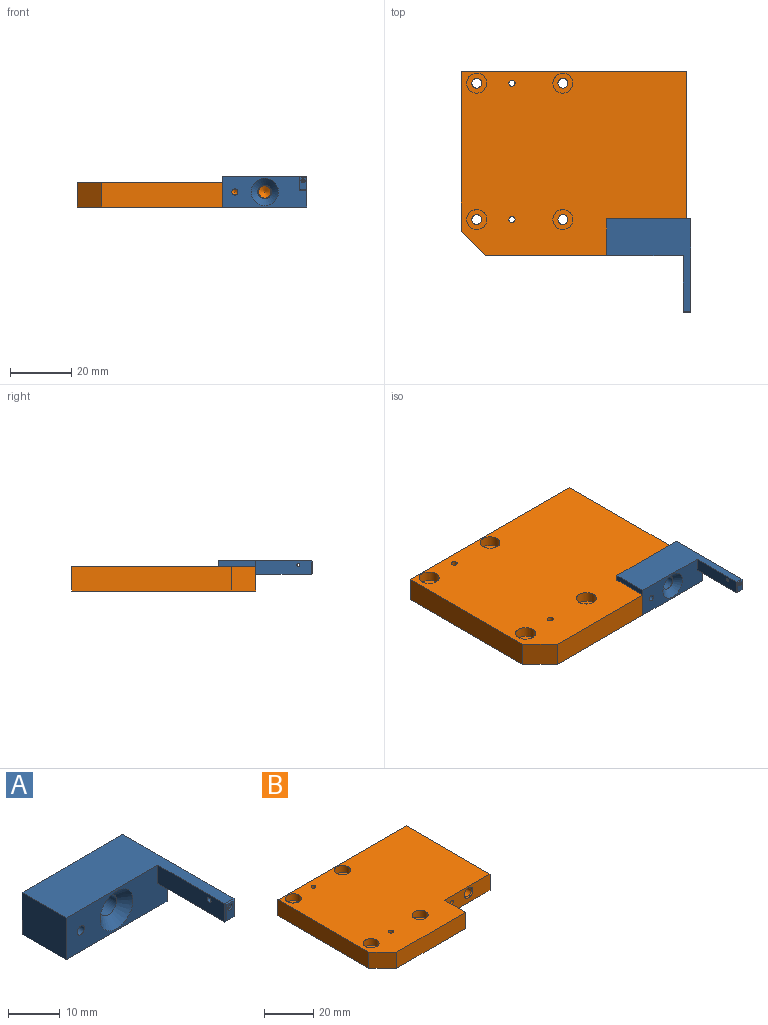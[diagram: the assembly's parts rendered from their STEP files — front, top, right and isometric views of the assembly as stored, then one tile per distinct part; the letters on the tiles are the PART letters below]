
ASSEMBLY  parts=2 mates=1
PART A: 21 faces, bbox 27.5x30.5x9.8 mm
  f0: plane 18.25x4.3mm, normal (-1,0,0), area 77.7mm2, adj f2,f7,f8,f10,f15
  f1: cylinder r=0.42mm len=3.99mm, axis (0,-1,0), area 10.3mm2, adj f9,f10
  f2: plane 27.5x9.8mm, normal (0,-1,0), area 192.6mm2, adj f0,f3,f5,f7,f8,f17,f19,f20
  f3: plane 30.25x9.8mm, normal (1,0,0), area 195.3mm2, adj f2,f4,f5,f7,f8,f10,f14
  f4: plane 27.5x9.8mm, normal (0,1,0), area 250.5mm2, adj f3,f5,f7,f17,f18,f20
  f5: plane 27.5x12mm, normal (0,0,-1), area 330mm2, adj f2,f3,f4,f17
  f6: plane 3.8x2mm, normal (0,-1,0), area 6.2mm2, adj f9,f13,f14,f15,f16
  f7: plane 30.25x27.5mm, normal (0,0,1), area 375.6mm2, adj f0,f2,f3,f4,f13,f17
  f8: plane 18.25x2.5mm, normal (0,0,-1), area 45.6mm2, adj f0,f2,f3,f16
  f9: cone r=0.42mm half-angle=45deg, axis (0,-1,0), area 1.2mm2, adj f1,f6
  f10: cylinder r=0.5mm len=2.5mm, axis (-1,0,0), area 6.6mm2, adj f0,f1,f3,f12
  f11: cone r=0mm half-angle=59deg, axis (0,-1,0), area 0.7mm2, adj f12
  f12: cylinder r=0.42mm len=0.85mm, axis (0,-1,0), area 1.6mm2, adj f10,f11
  f13: plane 2.5x0.25mm, normal (0,-0.71,0.71), area 0.8mm2, adj f6,f7,f14,f15
  f14: plane 4.3x0.25mm, normal (0.71,-0.71,0), area 1.4mm2, adj f3,f6,f13,f16
  f15: plane 4.3x0.25mm, normal (-0.71,-0.71,0), area 1.4mm2, adj f0,f6,f13,f16
  f16: plane 2.5x0.25mm, normal (0,-0.71,-0.71), area 0.8mm2, adj f6,f8,f14,f15
  f17: plane 12x9.8mm, normal (-1,0,0), area 117.6mm2, adj f2,f4,f5,f7
  f18: cylinder r=2.25mm len=9.77mm, axis (0,-1,0), area 138.1mm2, adj f4,f19
  f19: cone r=2.25mm half-angle=45deg, axis (0,-1,0), area 66.7mm2, adj f2,f18
  f20: cylinder r=1mm len=12mm, axis (0,-1,0), area 75.4mm2, adj f2,f4
PART B: 28 faces, bbox 73.5x60x8 mm
  f0: plane 73.5x60mm, normal (0,0,-1), area 4027.5mm2, adj f2,f3,f4,f5,f6,f7,f10,f13
  f1: plane 73.5x60mm, normal (0,0,1), area 3927mm2, adj f2,f3,f4,f5,f6,f9,f12,f15
  f2: plane 39.5x8mm, normal (0,-1,0), area 316mm2, adj f0,f1,f6,f22
  f3: plane 48x8mm, normal (1,0,0), area 384mm2, adj f0,f1,f4,f21
  f4: plane 73.5x8mm, normal (0,1,0), area 588mm2, adj f0,f1,f3,f5
  f5: plane 52x8mm, normal (-1,0,0), area 416mm2, adj f0,f1,f4,f6
  f6: plane 8x8mm, normal (-0.71,-0.71,0), area 90.5mm2, adj f0,f1,f2,f5
  f7: cylinder r=1.6mm len=4.6mm, axis (0,0,1), area 46.2mm2, adj f0,f8
  f8: plane 6.5x6.5mm, normal (0,0,1), area 25.1mm2, adj f7,f9
  f9: cylinder r=3.25mm len=6.5mm, axis (0,0,1), area 69.4mm2, adj f1,f8
  f10: cylinder r=1.6mm len=4.6mm, axis (0,0,1), area 46.2mm2, adj f0,f11
  f11: plane 6.5x6.5mm, normal (0,0,1), area 25.1mm2, adj f10,f12
  f12: cylinder r=3.25mm len=6.5mm, axis (0,0,1), area 69.4mm2, adj f1,f11
  f13: cylinder r=1.6mm len=4.6mm, axis (0,0,1), area 46.2mm2, adj f0,f14
  f14: plane 6.5x6.5mm, normal (0,0,1), area 25.1mm2, adj f13,f15
  f15: cylinder r=3.25mm len=6.5mm, axis (0,0,1), area 69.4mm2, adj f1,f14
  f16: cylinder r=1.6mm len=4.6mm, axis (0,0,1), area 46.2mm2, adj f0,f17
  f17: plane 6.5x6.5mm, normal (0,0,1), area 25.1mm2, adj f16,f18
  f18: cylinder r=3.25mm len=6.5mm, axis (0,0,1), area 69.4mm2, adj f1,f17
  f19: cylinder r=1mm len=8mm, axis (0,0,1), area 50.3mm2, adj f0,f1
  f20: cylinder r=1mm len=8mm, axis (0,0,1), area 50.3mm2, adj f0,f1
  f21: plane 26x8mm, normal (0,-1,0), area 185.2mm2, adj f0,f1,f3,f22,f24,f27
  f22: plane 12x8mm, normal (1,0,0), area 96mm2, adj f0,f1,f2,f21
  f23: cone r=0mm half-angle=59deg, axis (0,-1,0), area 3.7mm2, adj f24
  f24: cylinder r=1mm len=5.5mm, axis (0,-1,0), area 34.6mm2, adj f21,f23
  f25: cone r=0mm half-angle=59deg, axis (0,-1,0), area 14.7mm2, adj f26
  f26: cylinder r=2mm len=9.5mm, axis (0,-1,0), area 119.4mm2, adj f25,f27
  f27: cone r=2mm half-angle=45deg, axis (0,-1,0), area 10mm2, adj f21,f26
PLACE A t=(-16.18,3.37,19.07)mm
PLACE B t=(-16.18,3.37,19.07)mm
MATE cylindrical A.f20 <-> B.f23  axis (0,1,0) through (-2.18,-14.63,23.97)mm
